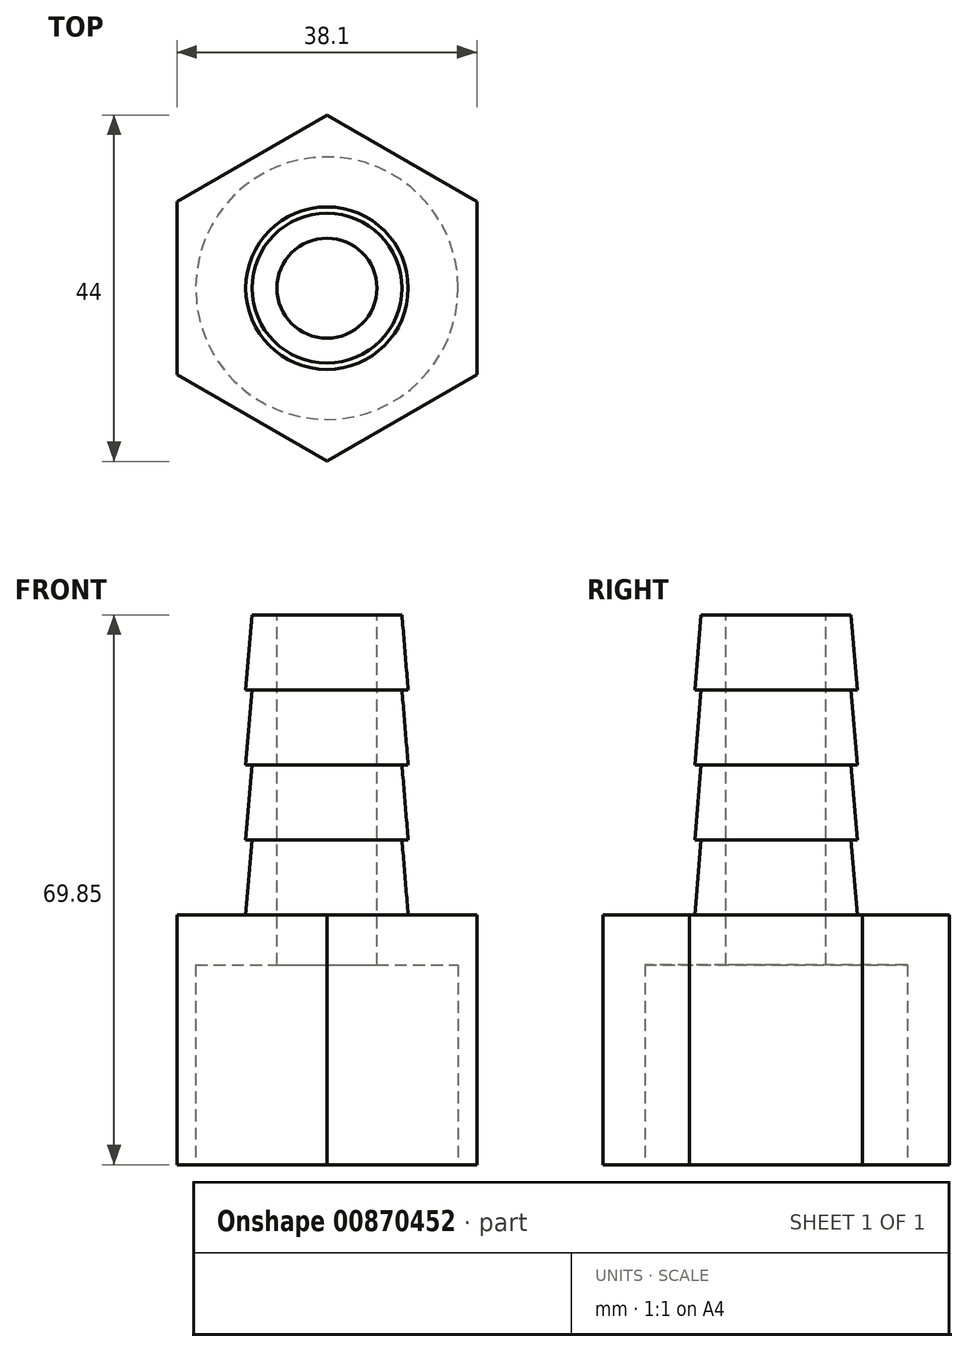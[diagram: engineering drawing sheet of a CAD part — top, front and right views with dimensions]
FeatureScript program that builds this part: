
annotation { "Feature Type Name" : "Feature", "Feature Type Description" : "" }
export const myFeature = defineFeature(function(context is Context, id is Id, definition is map)
    precondition{}
    {
        {
            var Q0;
            Q0=qCreatedBy(makeId("Top.planeOp"),FACE);
            var sketch = newSketch(context, id + "F0", { "sketchPlane" : qUnion([Q0])});
            skCircle(sketch, "E0.cCircle", {"center": v(0, 0) * mm, "radius": 19.05 * mm, "construction": true});
            skLineSegment(sketch, "E0.0", {"start": v(0, 22) * mm, "end": v(19.05, 11) * mm});
            skLineSegment(sketch, "E0.1", {"start": v(19.05, 11) * mm, "end": v(19.05, -11) * mm});
            skLineSegment(sketch, "E0.2", {"start": v(19.05, -11) * mm, "end": v(0, -22) * mm});
            skLineSegment(sketch, "E0.3", {"start": v(0, -22) * mm, "end": v(-19.05, -11) * mm});
            skLineSegment(sketch, "E0.4", {"start": v(-19.05, -11) * mm, "end": v(-19.05, 11) * mm});
            skLineSegment(sketch, "E0.5", {"start": v(-19.05, 11) * mm, "end": v(0, 22) * mm});
            skPoint(sketch, "E0.0.midPoint", {"position": v(9.53, 16.5) * mm});
            skSolve(sketch);
        }
        {
            var Q0;
            Q0 = qSketchRegion(id + "F0", true);
            extrude(context, id + "F1", {"entities" : qUnion([Q0]), "depth" : 31.75 * mm, "offsetDistance" : 25.4 * mm});
        }
        {
            var Q0;
            Q0=qCreatedBy(makeId("Front.planeOp"),FACE);
            var sketch = newSketch(context, id + "F2", { "sketchPlane" : qUnion([Q0])});
            skLineSegment(sketch, "E1", {"start": v(0, 69.85) * mm, "end": v(0, 31.75) * mm});
            skLineSegment(sketch, "E2", {"start": v(0, 31.75) * mm, "end": v(-10.32, 31.75) * mm});
            skLineSegment(sketch, "E3", {"start": v(-9.53, 69.85) * mm, "end": v(0, 69.85) * mm});
            skLineSegment(sketch, "E4", {"start": v(-10.32, 41.28) * mm, "end": v(-9.52, 41.28) * mm});
            skLineSegment(sketch, "E5", {"start": v(-9.52, 41.27) * mm, "end": v(-10.32, 31.75) * mm});
            skLineSegment(sketch, "E6", {"start": v(-10.32, 41.27) * mm, "end": v(-9.52, 50.8) * mm});
            skLineSegment(sketch, "E7", {"start": v(-9.52, 50.8) * mm, "end": v(-10.32, 50.8) * mm});
            skLineSegment(sketch, "E8", {"start": v(-10.32, 50.8) * mm, "end": v(-9.52, 60.32) * mm});
            skLineSegment(sketch, "E9", {"start": v(-9.53, 60.32) * mm, "end": v(-10.32, 60.32) * mm});
            skLineSegment(sketch, "E10", {"start": v(-10.32, 60.32) * mm, "end": v(-9.53, 69.85) * mm});
            skSolve(sketch);
        }
        {
            var Q0;
            Q0 = qSketchRegion(id + "F2", true);
            var Q1;
            Q1=sQuery(id+"F2.wireOp",EDGE,"E1");
            revolve(context, id + "F3", {"operationType" : NewBodyOperationType.ADD, "surfaceOperationType" : NewSurfaceOperationType.NEW, "entities" : qUnion([Q0]), "axis" : qUnion([Q1]), "revolveType" : RevolveType.FULL});
        }
        {
            var Q0;
            Q0=makeQuery(id+"F3.opRevolve","SWEPT_FACE",FACE,{"disambiguationData":[OSD([sQuery(id+"F2.wireOp",EDGE,"E3")])]});
            var sketch = newSketch(context, id + "F4", { "sketchPlane" : qUnion([Q0])});
            skCircle(sketch, "E11", {"center": v(0, 0) * mm, "radius": 6.35 * mm});
            skSolve(sketch);
        }
        {
            var Q0;
            Q0 = qSketchRegion(id + "F4", true);
            extrude(context, id + "F5", {"entities" : qUnion([Q0]), "operationType" : NewBodyOperationType.REMOVE, "oppositeDirection" : true, "depth" : 101.6 * mm, "offsetDistance" : 25.4 * mm});
        }
        {
            var Q0;
            Q0=makeQuery(id+"F1.opExtrude","CAP_FACE",FACE,{"disambiguationData":[OSD([sQuery(id+"F0.wireOp",EDGE,"E0.0"),sQuery(id+"F0.wireOp",EDGE,"E0.1"),sQuery(id+"F0.wireOp",EDGE,"E0.2"),sQuery(id+"F0.wireOp",EDGE,"E0.3"),sQuery(id+"F0.wireOp",EDGE,"E0.4"),sQuery(id+"F0.wireOp",EDGE,"E0.5")])],"isStart":true});
            var sketch = newSketch(context, id + "F6", { "sketchPlane" : qUnion([Q0])});
            skCircle(sketch, "E12", {"center": v(0, 0) * mm, "radius": 16.67 * mm});
            skSolve(sketch);
        }
        {
            var Q0;
            Q0 = qSketchRegion(id + "F6", true);
            extrude(context, id + "F7", {"entities" : qUnion([Q0]), "operationType" : NewBodyOperationType.REMOVE, "oppositeDirection" : true, "depth" : 25.4 * mm, "offsetDistance" : 25.4 * mm});
        }
    });
